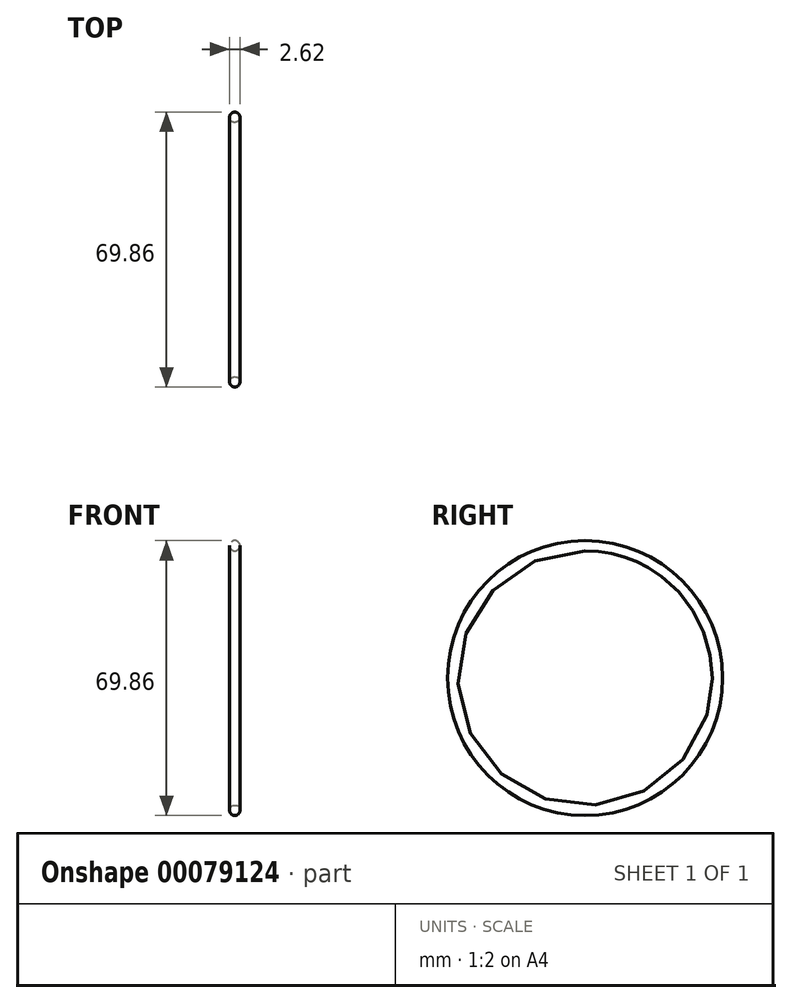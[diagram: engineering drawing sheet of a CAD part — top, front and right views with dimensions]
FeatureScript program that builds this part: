
annotation { "Feature Type Name" : "Feature", "Feature Type Description" : "" }
export const myFeature = defineFeature(function(context is Context, id is Id, definition is map)
    precondition{}
    {
        {
            var Q0;
            Q0=qCreatedBy(makeId("Front.planeOp"),FACE);
            var sketch = newSketch(context, id + "F0", { "sketchPlane" : qUnion([Q0])});
            skCircle(sketch, "E0", {"center": v(0, 33.62) * mm, "radius": 1.3 * mm});
            skLineSegment(sketch, "E1", {"start": v(-1.9, 0) * mm, "end": v(2.59, 0) * mm});
            skSolve(sketch);
        }
        {
            var Q0;
            Q0=makeQuery(id+"F0.imprint","IMPRINT",FACE,{"disambiguationData":[TD([[makeQuery(id+"F0.imprint","IMPRINT",EDGE,{"derivedFrom":sQuery(id+"F0.wireOp",EDGE,"E0")}),1.0]])]});
            var Q1;
            Q1=sQuery(id+"F0.wireOp",EDGE,"E1");
            revolve(context, id + "F1", {"entities" : qUnion([Q0]), "axis" : qUnion([Q1]), "revolveType" : RevolveType.FULL});
        }
    });
